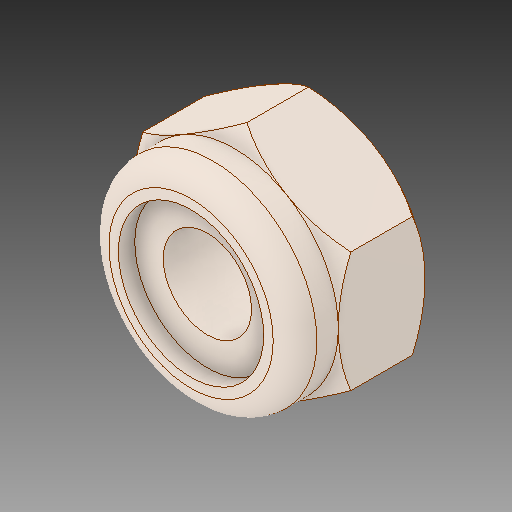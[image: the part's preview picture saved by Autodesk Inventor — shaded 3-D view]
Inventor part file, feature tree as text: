
AUTODESK INVENTOR PART (.ipt)
format: ipt  version: 2019 (Build 230136000, 136)  size: 167,424 bytes
history: native  units: in
note: dims shown in document units (in); Inventor stores cm internally (conversion verified against a paired STEP export)
features: fillet x1
ambient origin geometry x8: Origin, YZ Plane, XZ Plane, XY Plane, X Axis, Y Axis, Z Axis, Center Point
bodies: Solid1 (feature_tree)
feature tree (1):
  fillet  "Fillet1"  [1 undecoded]
note: 1 required parameter value undecoded (feature->parameter linkage not recoverable at this tier; creation-order binding heuristic only, values carry confidence <= 0.55)
